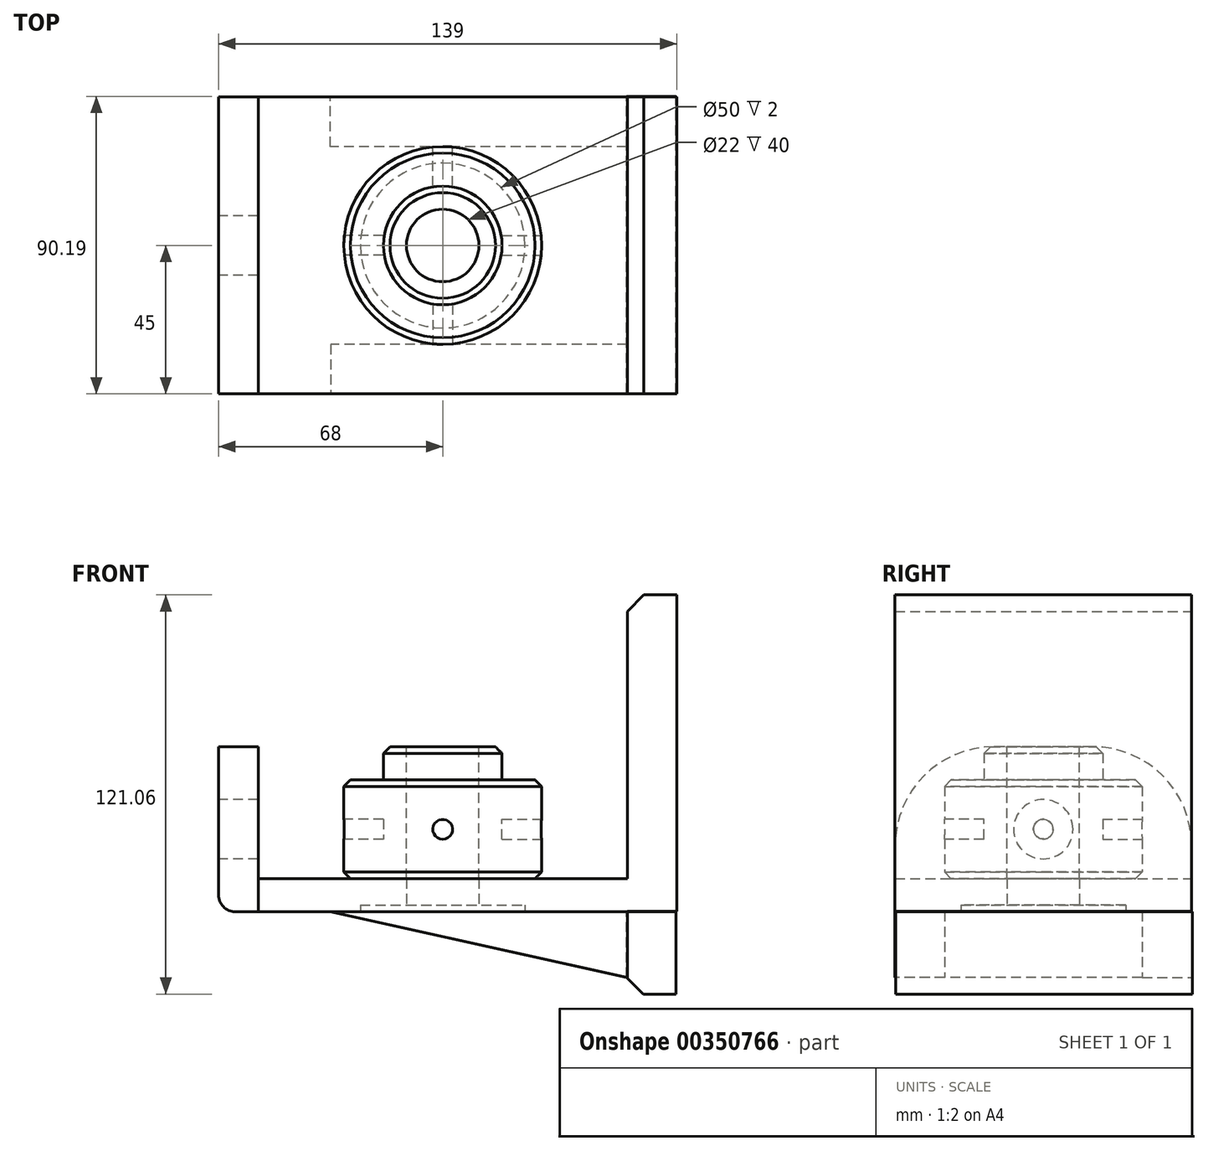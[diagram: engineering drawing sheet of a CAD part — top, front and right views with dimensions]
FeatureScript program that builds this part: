
annotation { "Feature Type Name" : "Feature", "Feature Type Description" : "" }
export const myFeature = defineFeature(function(context is Context, id is Id, definition is map)
    precondition{}
    {
        {
            var Q0;
            Q0=qCreatedBy(makeId("Top.planeOp"),FACE);
            var sketch = newSketch(context, id + "F0", { "sketchPlane" : qUnion([Q0])});
            skCircle(sketch, "E0", {"center": v(0, 0) * mm, "radius": 30 * mm});
            skSolve(sketch);
        }
        {
            var Q0;
            Q0 = qSketchRegion(id + "F0", true);
            extrude(context, id + "F1", {"entities" : qUnion([Q0]), "depth" : 30 * mm});
        }
        {
            var Q0;
            Q0=makeQuery(id+"F1.opExtrude","CAP_FACE",FACE,{"disambiguationData":[OSD([sQuery(id+"F0.wireOp",EDGE,"E0")])],"isStart":false});
            var sketch = newSketch(context, id + "F2", { "sketchPlane" : qUnion([Q0])});
            skCircle(sketch, "E1", {"center": v(0, 0) * mm, "radius": 18 * mm});
            skSolve(sketch);
        }
        {
            var Q0;
            Q0 = qSketchRegion(id + "F2", true);
            extrude(context, id + "F3", {"entities" : qUnion([Q0]), "operationType" : NewBodyOperationType.ADD, "depth" : 10 * mm});
        }
        {
            var Q0;
            Q0=makeQuery(id+"F3.opExtrude","CAP_EDGE",EDGE,{"disambiguationData":[OSD([sQuery(id+"F2.wireOp",EDGE,"E1")])],"isStart":false});
            var Q1;
            Q1=makeQuery(id+"F1.opExtrude","CAP_EDGE",EDGE,{"disambiguationData":[OSD([sQuery(id+"F0.wireOp",EDGE,"E0")])],"isStart":false});
            var Q2;
            Q2=makeQuery(id+"F1.opExtrude","CAP_EDGE",EDGE,{"disambiguationData":[OSD([sQuery(id+"F0.wireOp",EDGE,"E0")])],"isStart":true});
            chamfer(context, id + "F4", {"entities" : qUnion([Q0, Q1, Q2]), "width" : 2 * mm, "tangentPropagation" : true});
        }
        {
            var Q0;
            Q0=makeQuery(id+"F3.opExtrude","CAP_FACE",FACE,{"disambiguationData":[OSD([sQuery(id+"F2.wireOp",EDGE,"E1")])],"isStart":false});
            var sketch = newSketch(context, id + "F5", { "sketchPlane" : qUnion([Q0])});
            skCircle(sketch, "E2", {"center": v(0, 0) * mm, "radius": 11 * mm});
            skSolve(sketch);
        }
        {
            var Q0;
            Q0=makeQuery(id+"F5.imprint","IMPRINT",FACE,{"disambiguationData":[TD([[makeQuery(id+"F5.imprint","IMPRINT",EDGE,{"derivedFrom":sQuery(id+"F5.wireOp",EDGE,"E2")}),1.0]])]});
            extrude(context, id + "F6", {"entities" : qUnion([Q0]), "operationType" : NewBodyOperationType.REMOVE, "oppositeDirection" : true, "depth" : 40 * mm});
        }
        {
            var Q0;
            Q0=qCreatedBy(makeId("Right.planeOp"),FACE);
            cPlane(context, id + "F7", {"entities" : qUnion([Q0]), "cplaneType" : CPlaneType.OFFSET, "offset" : 30 * mm, "width" : 150 * mm, "height" : 150 * mm});
        }
        {
            var Q0;
            Q0=qCreatedBy(id+"F7.planeOp",FACE);
            var sketch = newSketch(context, id + "F8", { "sketchPlane" : qUnion([Q0])});
            skCircle(sketch, "E3", {"center": v(0, 15) * mm, "radius": 3 * mm});
            skSolve(sketch);
        }
        {
            var Q0;
            Q0 = qSketchRegion(id + "F8", true);
            extrude(context, id + "F9", {"entities" : qUnion([Q0]), "operationType" : NewBodyOperationType.REMOVE, "oppositeDirection" : true, "depth" : 12 * mm});
        }
        {
            var Q0;
            Q0=qCreatedBy(makeId("Right.planeOp"),FACE);
            cPlane(context, id + "F10", {"entities" : qUnion([Q0]), "cplaneType" : CPlaneType.OFFSET, "offset" : 30 * mm, "oppositeDirection" : true, "width" : 150 * mm, "height" : 150 * mm});
        }
        {
            var Q0;
            Q0=qCreatedBy(id+"F10.planeOp",FACE);
            var sketch = newSketch(context, id + "F11", { "sketchPlane" : qUnion([Q0])});
            skCircle(sketch, "E4", {"center": v(0, 15) * mm, "radius": 3 * mm});
            skSolve(sketch);
        }
        {
            var Q0;
            Q0 = qSketchRegion(id + "F11", true);
            extrude(context, id + "F12", {"entities" : qUnion([Q0]), "operationType" : NewBodyOperationType.REMOVE, "depth" : 12 * mm});
        }
        {
            var Q0;
            Q0=qCreatedBy(makeId("Front.planeOp"),FACE);
            cPlane(context, id + "F13", {"entities" : qUnion([Q0]), "cplaneType" : CPlaneType.OFFSET, "offset" : 30 * mm, "width" : 150 * mm, "height" : 150 * mm});
        }
        {
            var Q0;
            Q0=qCreatedBy(makeId("Front.planeOp"),FACE);
            cPlane(context, id + "F14", {"entities" : qUnion([Q0]), "cplaneType" : CPlaneType.OFFSET, "offset" : 30 * mm, "oppositeDirection" : true, "width" : 150 * mm, "height" : 150 * mm});
        }
        {
            var Q0;
            Q0=qCreatedBy(id+"F13.planeOp",FACE);
            var sketch = newSketch(context, id + "F15", { "sketchPlane" : qUnion([Q0])});
            skCircle(sketch, "E5", {"center": v(0, 15) * mm, "radius": 3 * mm});
            skSolve(sketch);
        }
        {
            var Q0;
            Q0 = qSketchRegion(id + "F15", true);
            extrude(context, id + "F16", {"entities" : qUnion([Q0]), "operationType" : NewBodyOperationType.REMOVE, "oppositeDirection" : true, "depth" : 12 * mm});
        }
        {
            var Q0;
            Q0=qCreatedBy(id+"F14.planeOp",FACE);
            var sketch = newSketch(context, id + "F17", { "sketchPlane" : qUnion([Q0])});
            skCircle(sketch, "E6", {"center": v(0, 15) * mm, "radius": 3 * mm});
            skSolve(sketch);
        }
        {
            var Q0;
            Q0=makeQuery(id+"F17.imprint","IMPRINT",FACE,{"disambiguationData":[TD([[makeQuery(id+"F17.imprint","IMPRINT",EDGE,{"derivedFrom":sQuery(id+"F17.wireOp",EDGE,"E6")}),1.0]])]});
            var Q1;
            Q1=sQuery(id+"F17.wireOp",EDGE,"E6");
            extrude(context, id + "F18", {"entities" : qUnion([Q0]), "operationType" : NewBodyOperationType.REMOVE, "surfaceEntities" : qUnion([Q1]), "depth" : 12 * mm});
        }
        {
            var Q0;
            Q0=qCreatedBy(id+"F10.planeOp",FACE);
            cPlane(context, id + "F19", {"entities" : qUnion([Q0]), "cplaneType" : CPlaneType.OFFSET, "offset" : 26 * mm, "oppositeDirection" : true, "width" : 150 * mm, "height" : 150 * mm});
        }
        {
            var Q0;
            Q0=qCreatedBy(id+"F19.planeOp",FACE);
            var sketch = newSketch(context, id + "F20", { "sketchPlane" : qUnion([Q0])});
            skPoint(sketch, "E7.middle", {"position": v(0, 15) * mm});
            skLineSegment(sketch, "E8.bottom", {"start": v(45, 40) * mm, "end": v(-45, 40) * mm});
            skLineSegment(sketch, "E8.top", {"start": v(45, -10) * mm, "end": v(-45, -10) * mm});
            skLineSegment(sketch, "E8.left", {"start": v(45, 40) * mm, "end": v(45, -10) * mm});
            skLineSegment(sketch, "E8.right", {"start": v(-45, 40) * mm, "end": v(-45, -10) * mm});
            skSolve(sketch);
        }
        {
            var Q0;
            Q0=makeQuery(id+"F20.imprint","IMPRINT",FACE,{"disambiguationData":[TD([[makeQuery(id+"F20.imprint","IMPRINT",EDGE,{"derivedFrom":sQuery(id+"F20.wireOp",EDGE,"E8.bottom")}),1.0]])]});
            extrude(context, id + "F21", {"entities" : qUnion([Q0]), "oppositeDirection" : true, "depth" : 12 * mm});
        }
        {
            var Q0;
            Q0=makeQuery(id+"F21.opExtrude","CAP_FACE",FACE,{"disambiguationData":[OSD([sQuery(id+"F20.wireOp",EDGE,"E8.bottom"),sQuery(id+"F20.wireOp",EDGE,"E8.top"),sQuery(id+"F20.wireOp",EDGE,"E8.left"),sQuery(id+"F20.wireOp",EDGE,"E8.right")])],"isStart":false});
            var sketch = newSketch(context, id + "F22", { "sketchPlane" : qUnion([Q0])});
            skCircle(sketch, "E9", {"center": v(0, 15) * mm, "radius": 9 * mm});
            skSolve(sketch);
        }
        {
            var Q0;
            Q0=makeQuery(id+"F22.imprint","IMPRINT",FACE,{"disambiguationData":[TD([[makeQuery(id+"F22.imprint","IMPRINT",EDGE,{"derivedFrom":sQuery(id+"F22.wireOp",EDGE,"E9")}),1.0]])]});
            extrude(context, id + "F23", {"entities" : qUnion([Q0]), "operationType" : NewBodyOperationType.REMOVE, "oppositeDirection" : true, "depth" : 12 * mm});
        }
        {
            var Q0;
            Q0=qCreatedBy(makeId("Top.planeOp"),FACE);
            cPlane(context, id + "F24", {"entities" : qUnion([Q0]), "cplaneType" : CPlaneType.OFFSET, "offset" : 10 * mm, "oppositeDirection" : true, "width" : 150 * mm, "height" : 150 * mm});
        }
        {
            var Q0;
            Q0=qCreatedBy(id+"F24.planeOp",FACE);
            var sketch = newSketch(context, id + "F25", { "sketchPlane" : qUnion([Q0])});
            skLineSegment(sketch, "E10.top", {"start": v(-56, 45) * mm, "end": v(56, 45) * mm});
            skLineSegment(sketch, "E10.left", {"start": v(-56, -45) * mm, "end": v(-56, 45) * mm});
            skLineSegment(sketch, "E10.right", {"start": v(56, -45) * mm, "end": v(56, 45) * mm});
            skPoint(sketch, "E10.middle", {"position": v(0, 0) * mm});
            skLineSegment(sketch, "E11", {"start": v(-56, -45) * mm, "end": v(56, -45) * mm});
            skSolve(sketch);
        }
        {
            var Q0;
            Q0 = qSketchRegion(id + "F25", true);
            extrude(context, id + "F26", {"entities" : qUnion([Q0]), "depth" : 10 * mm});
        }
        {
            var Q0;
            Q0=makeQuery(id+"F26.opExtrude","CAP_FACE",FACE,{"disambiguationData":[OSD([sQuery(id+"F25.wireOp",EDGE,"E10.top"),sQuery(id+"F25.wireOp",EDGE,"E10.left"),sQuery(id+"F25.wireOp",EDGE,"E10.right"),sQuery(id+"F25.wireOp",EDGE,"E11")])],"isStart":true});
            var sketch = newSketch(context, id + "F27", { "sketchPlane" : qUnion([Q0])});
            skCircle(sketch, "E12", {"center": v(0, 0) * mm, "radius": 25 * mm});
            skSolve(sketch);
        }
        {
            var Q0;
            Q0=makeQuery(id+"F27.imprint","IMPRINT",FACE,{"disambiguationData":[TD([[makeQuery(id+"F27.imprint","IMPRINT",EDGE,{"derivedFrom":sQuery(id+"F27.wireOp",EDGE,"E12")}),1.0]])]});
            extrude(context, id + "F28", {"entities" : qUnion([Q0]), "operationType" : NewBodyOperationType.REMOVE, "oppositeDirection" : true, "depth" : 2 * mm});
        }
        {
            var Q0;
            Q0=makeQuery(id+"F28.boolean.opBoolean","COPY",FACE,{"derivedFrom":makeQuery(id+"F28.opExtrude","CAP_FACE",FACE,{"disambiguationData":[OSD([sQuery(id+"F27.wireOp",EDGE,"E12")])],"isStart":false})});
            var sketch = newSketch(context, id + "F29", { "sketchPlane" : qUnion([Q0])});
            skCircle(sketch, "E13", {"center": v(0, 0) * mm, "radius": 11 * mm});
            skSolve(sketch);
        }
        {
            var Q0;
            Q0 = qSketchRegion(id + "F29", true);
            extrude(context, id + "F30", {"entities" : qUnion([Q0]), "operationType" : NewBodyOperationType.REMOVE, "oppositeDirection" : true, "depth" : 8 * mm});
        }
        {
            var Q0;
            Q0=makeQuery(id+"F21.opExtrude","SWEPT_EDGE",EDGE,{"disambiguationData":[OSD([sQuery(id+"F20.wireOp",EDGE,"E8.bottom"),sQuery(id+"F20.wireOp",EDGE,"E8.left")])]});
            fillet(context, id + "F31", {"entities" : qUnion([Q0]), "radius" : 30 * mm, "tangentPropagation" : true, "allowEdgeOverflow" : false});
        }
        {
            var Q0;
            Q0=makeQuery(id+"F21.opExtrude","SWEPT_EDGE",EDGE,{"disambiguationData":[OSD([sQuery(id+"F20.wireOp",EDGE,"E8.bottom"),sQuery(id+"F20.wireOp",EDGE,"E8.right")])]});
            fillet(context, id + "F32", {"entities" : qUnion([Q0]), "radius" : 30 * mm, "tangentPropagation" : true, "allowEdgeOverflow" : false});
        }
        {
            var Q0;
            Q0=qCreatedBy(makeId("Right.planeOp"),FACE);
            cPlane(context, id + "F33", {"entities" : qUnion([Q0]), "cplaneType" : CPlaneType.OFFSET, "offset" : 56 * mm, "width" : 150 * mm, "height" : 150 * mm});
        }
        {
            var Q0;
            Q0=qCreatedBy(id+"F33.planeOp",FACE);
            var sketch = newSketch(context, id + "F34", { "sketchPlane" : qUnion([Q0])});
            skPoint(sketch, "E14.middle", {"position": v(0, 0) * mm});
            skLineSegment(sketch, "E15", {"start": v(-45, -9.94) * mm, "end": v(45, -9.94) * mm});
            skPoint(sketch, "E14.top.start.orphan", {"position": v(-45, -56.06) * mm});
            skPoint(sketch, "E16.orphan", {"position": v(45, -56.06) * mm});
            skLineSegment(sketch, "E17.0", {"start": v(-45, 86.06) * mm, "end": v(45, 86.06) * mm});
            skLineSegment(sketch, "E18", {"start": v(45, 86.06) * mm, "end": v(45, -9.94) * mm});
            skLineSegment(sketch, "E19", {"start": v(-45, 86.06) * mm, "end": v(-45, -9.94) * mm});
            skSolve(sketch);
        }
        {
            var Q0;
            Q0=qCreatedBy(id+"F24.planeOp",FACE);
            var sketch = newSketch(context, id + "F35", { "sketchPlane" : qUnion([Q0])});
            skLineSegment(sketch, "E20.bottom", {"start": v(55.84, -44.81) * mm, "end": v(70.84, -44.81) * mm});
            skLineSegment(sketch, "E20.top", {"start": v(55.84, 45.19) * mm, "end": v(70.84, 45.19) * mm});
            skLineSegment(sketch, "E20.left", {"start": v(55.84, -44.81) * mm, "end": v(55.84, 45.19) * mm});
            skLineSegment(sketch, "E20.right", {"start": v(70.84, -44.81) * mm, "end": v(70.84, 45.19) * mm});
            skSolve(sketch);
        }
        {
            var Q0;
            Q0 = qSketchRegion(id + "F35", true);
            extrude(context, id + "F36", {"entities" : qUnion([Q0]), "operationType" : NewBodyOperationType.ADD, "oppositeDirection" : true, "depth" : 25 * mm});
        }
        {
            var Q0;
            Q0=makeQuery(id+"F34.imprint","IMPRINT",FACE,{"disambiguationData":[TD([[makeQuery(id+"F34.imprint","IMPRINT",EDGE,{"derivedFrom":sQuery(id+"F34.wireOp",EDGE,"E15")}),1.0]])]});
            extrude(context, id + "F37", {"entities" : qUnion([Q0]), "operationType" : NewBodyOperationType.ADD, "depth" : 15 * mm});
        }
        {
            var Q0;
            Q0=makeQuery(id+"F37.opExtrude","CAP_EDGE",EDGE,{"disambiguationData":[OSD([sQuery(id+"F34.wireOp",EDGE,"E17.0")])],"isStart":true});
            chamfer(context, id + "F38", {"entities" : qUnion([Q0]), "width" : 5 * mm, "tangentPropagation" : true});
        }
        {
            var Q0;
            Q0=makeQuery(id+"F36.opExtrude","CAP_EDGE",EDGE,{"disambiguationData":[OSD([sQuery(id+"F35.wireOp",EDGE,"E20.left")])],"isStart":false});
            chamfer(context, id + "F39", {"entities" : qUnion([Q0]), "width" : 5 * mm, "tangentPropagation" : true});
        }
        {
            var Q0;
            Q0=makeQuery(id+"F21.opExtrude","CAP_EDGE",EDGE,{"disambiguationData":[OSD([sQuery(id+"F20.wireOp",EDGE,"E8.top")])],"isStart":false});
            fillet(context, id + "F40", {"entities" : qUnion([Q0]), "radius" : 5 * mm, "tangentPropagation" : true, "allowEdgeOverflow" : false});
        }
        {
            var Q0;
            Q0=qCreatedBy(makeId("Front.planeOp"),FACE);
            cPlane(context, id + "F41", {"entities" : qUnion([Q0]), "cplaneType" : CPlaneType.OFFSET, "offset" : 45 * mm, "width" : 150 * mm, "height" : 150 * mm});
        }
        {
            var Q0;
            Q0=qCreatedBy(makeId("Front.planeOp"),FACE);
            cPlane(context, id + "F42", {"entities" : qUnion([Q0]), "cplaneType" : CPlaneType.OFFSET, "offset" : 45 * mm, "oppositeDirection" : true, "width" : 150 * mm, "height" : 150 * mm});
        }
        {
            var Q0;
            Q0=qCreatedBy(id+"F42.planeOp",FACE);
            var sketch = newSketch(context, id + "F43", { "sketchPlane" : qUnion([Q0])});
            skLineSegment(sketch, "E21", {"start": v(55.84, -10) * mm, "end": v(-34.16, -10) * mm});
            skLineSegment(sketch, "E22", {"start": v(55.84, -10) * mm, "end": v(55.84, -30) * mm});
            skLineSegment(sketch, "E23", {"start": v(55.84, -30) * mm, "end": v(-34.16, -10) * mm});
            skSolve(sketch);
        }
        {
            var Q0;
            Q0 = qSketchRegion(id + "F43", true);
            extrude(context, id + "F44", {"entities" : qUnion([Q0]), "operationType" : NewBodyOperationType.ADD, "depth" : 15 * mm});
        }
        {
            var Q0;
            Q0=qCreatedBy(id+"F41.planeOp",FACE);
            var sketch = newSketch(context, id + "F45", { "sketchPlane" : qUnion([Q0])});
            skLineSegment(sketch, "E24", {"start": v(56, -10) * mm, "end": v(56, -30) * mm});
            skLineSegment(sketch, "E25", {"start": v(56, -10) * mm, "end": v(-34, -10) * mm});
            skLineSegment(sketch, "E26", {"start": v(-34, -10) * mm, "end": v(56, -30) * mm});
            skSolve(sketch);
        }
        {
            var Q0;
            Q0 = qSketchRegion(id + "F45", true);
            extrude(context, id + "F46", {"entities" : qUnion([Q0]), "oppositeDirection" : true, "depth" : 15 * mm});
        }
    });
